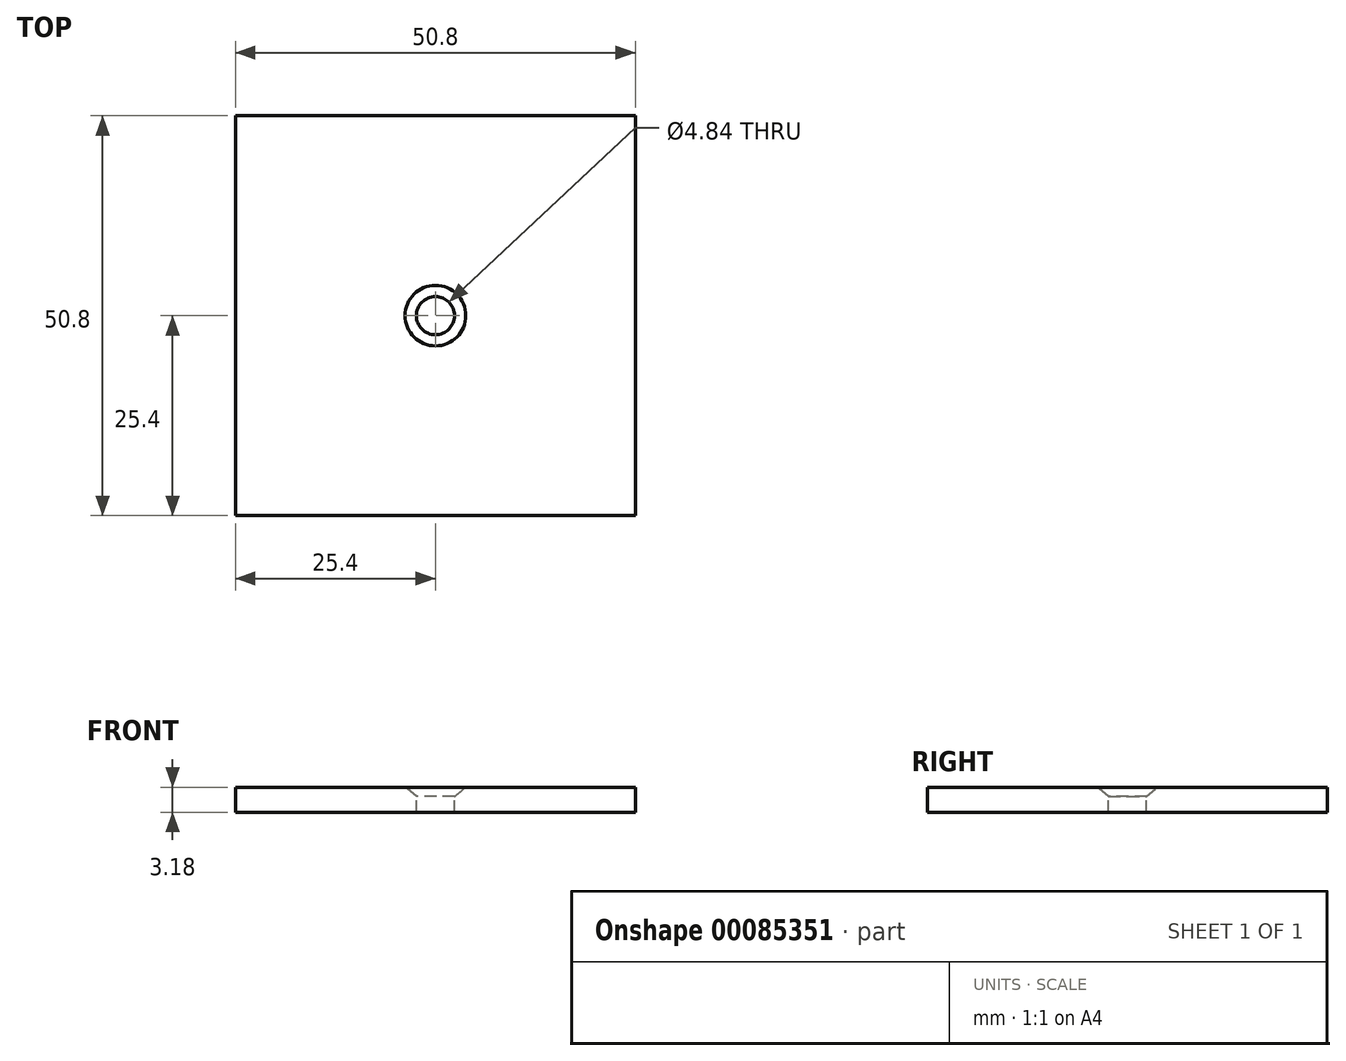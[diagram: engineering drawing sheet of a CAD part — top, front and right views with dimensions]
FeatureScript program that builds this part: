
annotation { "Feature Type Name" : "Feature", "Feature Type Description" : "" }
export const myFeature = defineFeature(function(context is Context, id is Id, definition is map)
    precondition{}
    {
        {
            var Q0;
            Q0=qCreatedBy(makeId("Top.planeOp"),FACE);
            var sketch = newSketch(context, id + "F0", { "sketchPlane" : qUnion([Q0])});
            skLineSegment(sketch, "E0.bottom", {"start": v(-25.4, 25.4) * mm, "end": v(25.4, 25.4) * mm});
            skLineSegment(sketch, "E0.top", {"start": v(-25.4, -25.4) * mm, "end": v(25.4, -25.4) * mm});
            skLineSegment(sketch, "E0.left", {"start": v(-25.4, 25.4) * mm, "end": v(-25.4, -25.4) * mm});
            skLineSegment(sketch, "E0.right", {"start": v(25.4, 25.4) * mm, "end": v(25.4, -25.4) * mm});
            skPoint(sketch, "E0.middle", {"position": v(0, 0) * mm});
            skSolve(sketch);
        }
        {
            var Q0;
            Q0=makeQuery(id+"F0.imprint","IMPRINT",FACE,{"disambiguationData":[TD([[makeQuery(id+"F0.imprint","IMPRINT",EDGE,{"derivedFrom":sQuery(id+"F0.wireOp",EDGE,"E0.bottom")}),-1.0]])]});
            extrude(context, id + "F1", {"entities" : qUnion([Q0]), "oppositeDirection" : true, "depth" : 3.17 * mm, "offsetDistance" : 25.4 * mm});
        }
        {
            var Q0;
            Q0=sQuery(id+"F0.wireOp",VERTEX,"E0.middle");
            var Q1;
            Q1=makeQuery(id+"F1.opExtrude","SWEPT_BODY",BODY,{"disambiguationData":[OSD([sQuery(id+"F0.wireOp",EDGE,"E0.bottom"),sQuery(id+"F0.wireOp",EDGE,"E0.top"),sQuery(id+"F0.wireOp",EDGE,"E0.left"),sQuery(id+"F0.wireOp",EDGE,"E0.right")])]});
            hole(context, id + "F2", {"style" : HoleStyle.C_SINK, "endStyle" : HoleEndStyle.THROUGH, "holeDiameter" : 4.84 * mm, "cSinkDiameter" : 7.7 * mm, "cSinkAngle" : 100 * degree, "majorDiameter" : 6.35 * mm, "tappedDepth" : 12.7 * mm, "tapClearance" : 3, "startFromSketch" : true, "locations" : qUnion([Q0]), "scope" : qUnion([Q1])});
        }
    });
